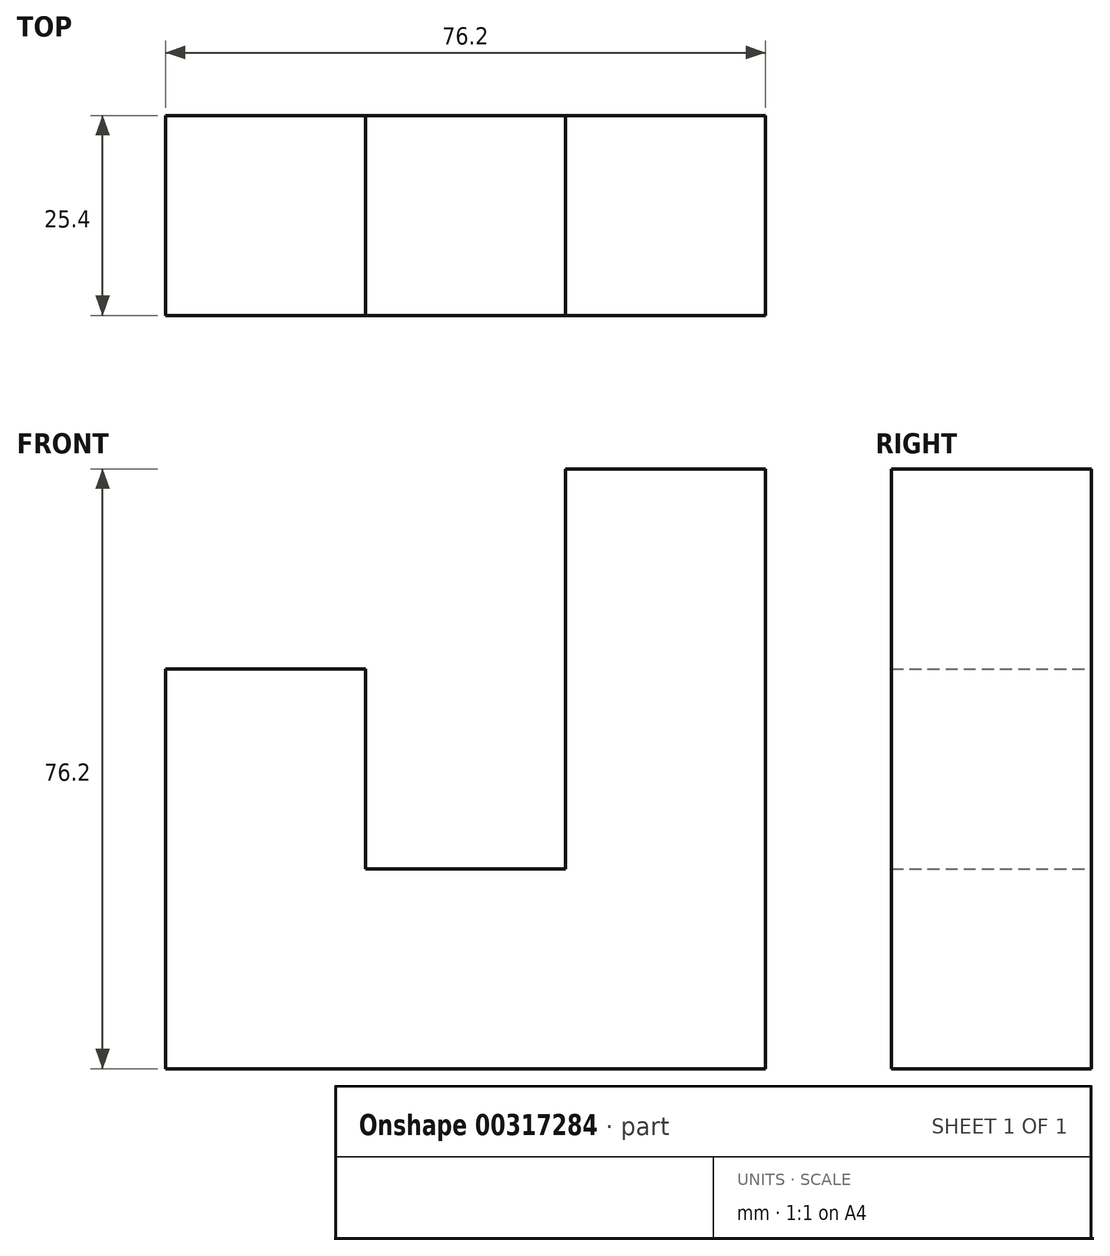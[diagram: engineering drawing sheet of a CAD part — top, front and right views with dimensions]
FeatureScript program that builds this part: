
annotation { "Feature Type Name" : "Feature", "Feature Type Description" : "" }
export const myFeature = defineFeature(function(context is Context, id is Id, definition is map)
    precondition{}
    {
        {
            var Q0;
            Q0=qCreatedBy(makeId("Front.planeOp"),FACE);
            var sketch = newSketch(context, id + "F0", { "sketchPlane" : qUnion([Q0])});
            skLineSegment(sketch, "E0", {"start": v(-51.25, -34.73) * mm, "end": v(24.95, -34.73) * mm});
            skLineSegment(sketch, "E1", {"start": v(-0.45, 41.47) * mm, "end": v(-0.45, -9.33) * mm});
            skLineSegment(sketch, "E2", {"start": v(-0.45, -9.33) * mm, "end": v(-25.85, -9.33) * mm});
            skLineSegment(sketch, "E3", {"start": v(-25.85, -9.33) * mm, "end": v(-25.85, 16.07) * mm});
            skLineSegment(sketch, "E4", {"start": v(-25.85, 16.07) * mm, "end": v(-51.25, 16.07) * mm});
            skLineSegment(sketch, "E5", {"start": v(-51.25, 16.07) * mm, "end": v(-51.25, -34.73) * mm});
            skLineSegment(sketch, "E6", {"start": v(-0.45, 41.47) * mm, "end": v(24.95, 41.47) * mm});
            skLineSegment(sketch, "E7", {"start": v(24.95, 41.47) * mm, "end": v(24.95, -34.73) * mm});
            skSolve(sketch);
        }
        {
            var Q0;
            Q0=makeQuery(id+"F0.imprint","IMPRINT",FACE,{"disambiguationData":[TD([[makeQuery(id+"F0.imprint","IMPRINT",EDGE,{"derivedFrom":sQuery(id+"F0.wireOp",EDGE,"E0")}),1.0]])]});
            extrude(context, id + "F1", {"entities" : qUnion([Q0]), "depth" : 25.4 * mm});
        }
    });
